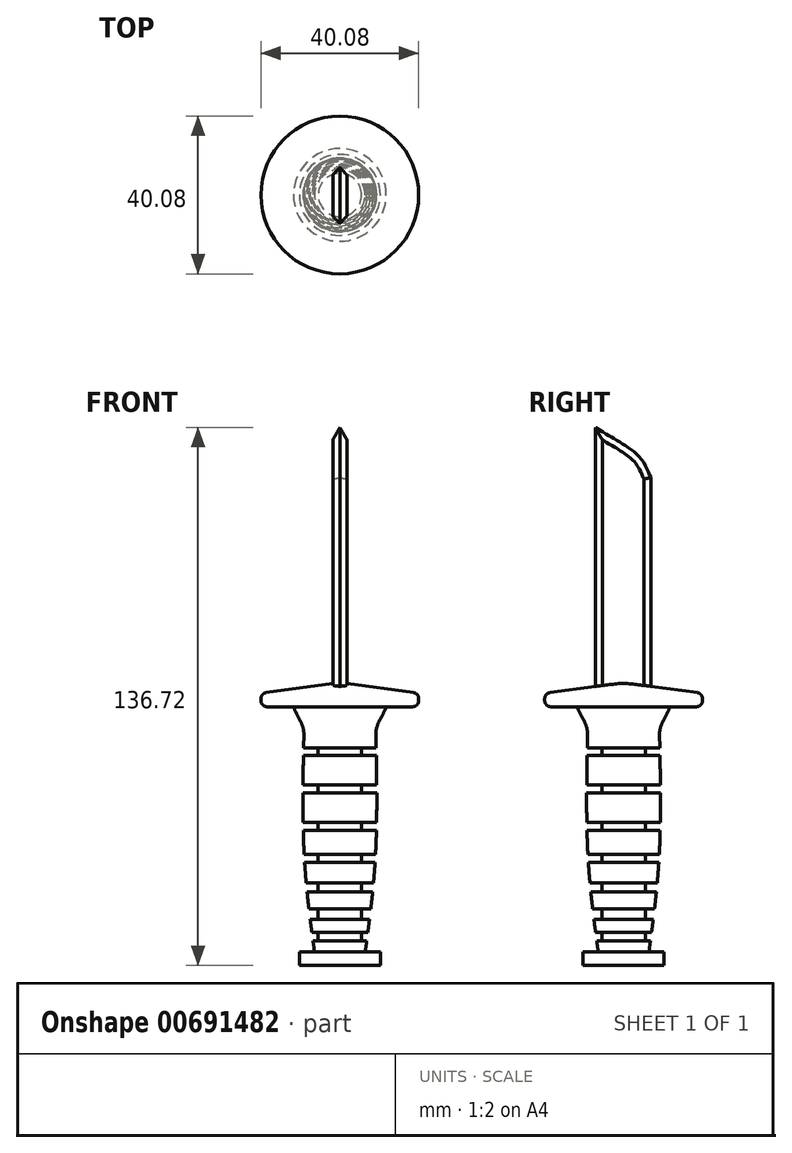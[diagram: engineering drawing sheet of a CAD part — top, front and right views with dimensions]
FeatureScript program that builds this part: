
annotation { "Feature Type Name" : "Feature", "Feature Type Description" : "" }
export const myFeature = defineFeature(function(context is Context, id is Id, definition is map)
    precondition{}
    {
        {
            var Q0;
            Q0=qCreatedBy(makeId("Front.planeOp"),FACE);
            var sketch = newSketch(context, id + "F0", { "sketchPlane" : qUnion([Q0])});
            skLineSegment(sketch, "E0", {"start": v(0, 79.4) * mm, "end": v(0, -77.48) * mm, "construction": true});
            skLineSegment(sketch, "E1", {"start": v(0, 41.4) * mm, "end": v(-13.25, 41.4) * mm});
            skLineSegment(sketch, "E2", {"start": v(-13.25, 41.4) * mm, "end": v(-13.25, 37.56) * mm});
            skLineSegment(sketch, "E3", {"start": v(-13.25, 37.56) * mm, "end": v(-9.06, 33.56) * mm});
            skFitSpline(sketch, "E4", {"points": [v(-9.06, 33.56) * mm, v(-9.06, 0) * mm, v(-6.45, -24.67) * mm], "startDerivative": vector(-1.52, -64.84) * mm, "endDerivative": vector(6.96, -51.26) * mm});
            skLineSegment(sketch, "E5", {"start": v(-6.45, -24.67) * mm, "end": v(-10.28, -24.67) * mm});
            skLineSegment(sketch, "E6", {"start": v(-10.28, -24.67) * mm, "end": v(-10.28, -28.15) * mm});
            skLineSegment(sketch, "E7", {"start": v(-10.28, -28.15) * mm, "end": v(0, -28.15) * mm});
            skLineSegment(sketch, "E8", {"start": v(0, -28.15) * mm, "end": v(0, 41.4) * mm});
            skSolve(sketch);
        }
        {
            var Q0;
            Q0 = qSketchRegion(id + "F0", true);
            var Q1;
            Q1=sQuery(id+"F0.wireOp",EDGE,"E8");
            revolve(context, id + "F1", {"entities" : qUnion([Q0]), "axis" : qUnion([Q1]), "revolveType" : RevolveType.FULL});
        }
        {
            var Q0;
            Q0=qCreatedBy(makeId("Right.planeOp"),FACE);
            var sketch = newSketch(context, id + "F2", { "sketchPlane" : qUnion([Q0])});
            skLineSegment(sketch, "E9", {"start": v(7.44, 35.34) * mm, "end": v(7.44, 95.92) * mm});
            skFitSpline(sketch, "E10", {"points": [v(7.44, 95.92) * mm, v(4.1, 101.72) * mm, v(-7.71, 109.53) * mm], "startDerivative": vector(-6.13, 12.4) * mm, "endDerivative": vector(-14.92, 10.78) * mm});
            skLineSegment(sketch, "E11", {"start": v(-7.71, 109.53) * mm, "end": v(-7.71, 35.27) * mm});
            skLineSegment(sketch, "E12", {"start": v(-7.71, 35.27) * mm, "end": v(7.44, 35.34) * mm});
            skSolve(sketch);
        }
        {
            var Q0;
            Q0 = qSketchRegion(id + "F2", true);
            extrude(context, id + "F3", {"entities" : qUnion([Q0]), "operationType" : NewBodyOperationType.ADD, "endBound" : BoundingType.SYMMETRIC, "depth" : 3.56 * mm, "offsetDistance" : 25.4 * mm});
        }
        {
            var Q0;
            Q0=makeQuery(id+"F3.opExtrude","CAP_EDGE",EDGE,{"disambiguationData":[OSD([sQuery(id+"F2.wireOp",EDGE,"E9")])],"isStart":true});
            var Q1;
            Q1=makeQuery(id+"F3.opExtrude","CAP_EDGE",EDGE,{"disambiguationData":[OSD([sQuery(id+"F2.wireOp",EDGE,"E9")])],"isStart":false});
            chamfer(context, id + "F4", {"entities" : qUnion([Q0, Q1]), "width" : 2.3 * mm, "tangentPropagation" : true});
        }
        {
            var Q0;
            Q0=makeQuery(id+"F3.opExtrude","CAP_EDGE",EDGE,{"disambiguationData":[OSD([sQuery(id+"F2.wireOp",EDGE,"E10")])],"isStart":true});
            var Q1;
            Q1=makeQuery(id+"F3.opExtrude","CAP_EDGE",EDGE,{"disambiguationData":[OSD([sQuery(id+"F2.wireOp",EDGE,"E10")])],"isStart":false});
            chamfer(context, id + "F5", {"entities" : qUnion([Q0, Q1]), "width" : 2.3 * mm, "tangentPropagation" : true});
        }
        {
            var Q0;
            Q0=makeQuery(id+"F3.opExtrude","CAP_EDGE",EDGE,{"disambiguationData":[OSD([sQuery(id+"F2.wireOp",EDGE,"E11")])],"isStart":false});
            var Q1;
            Q1=makeQuery(id+"F3.opExtrude","CAP_EDGE",EDGE,{"disambiguationData":[OSD([sQuery(id+"F2.wireOp",EDGE,"E11")])],"isStart":true});
            chamfer(context, id + "F6", {"entities" : qUnion([Q0, Q1]), "width" : 2.3 * mm, "tangentPropagation" : true});
        }
        {
            var Q0;
            Q0=qCreatedBy(makeId("Front.planeOp"),FACE);
            var sketch = newSketch(context, id + "F7", { "sketchPlane" : qUnion([Q0])});
            skLineSegment(sketch, "E13.bottom", {"start": v(-12.37, 27.05) * mm, "end": v(-5.5, 27.05) * mm});
            skLineSegment(sketch, "E13.top", {"start": v(-12.37, 25.15) * mm, "end": v(-5.5, 25.15) * mm});
            skLineSegment(sketch, "E13.left", {"start": v(-12.37, 27.05) * mm, "end": v(-12.37, 25.15) * mm});
            skLineSegment(sketch, "E13.right", {"start": v(-5.5, 27.05) * mm, "end": v(-5.5, 25.15) * mm});
            skLineSegment(sketch, "E14.bottom", {"start": v(-12.37, 17.75) * mm, "end": v(-5.5, 17.75) * mm});
            skLineSegment(sketch, "E14.top", {"start": v(-12.37, 15.74) * mm, "end": v(-5.5, 15.74) * mm});
            skLineSegment(sketch, "E14.left", {"start": v(-12.37, 17.75) * mm, "end": v(-12.37, 15.74) * mm});
            skLineSegment(sketch, "E14.right", {"start": v(-5.5, 17.75) * mm, "end": v(-5.5, 15.74) * mm});
            skLineSegment(sketch, "E15.bottom", {"start": v(-12.37, 8.23) * mm, "end": v(-5.5, 8.23) * mm});
            skLineSegment(sketch, "E15.top", {"start": v(-12.37, 6.12) * mm, "end": v(-5.5, 6.12) * mm});
            skLineSegment(sketch, "E15.left", {"start": v(-12.37, 8.23) * mm, "end": v(-12.37, 6.12) * mm});
            skLineSegment(sketch, "E15.right", {"start": v(-5.5, 8.23) * mm, "end": v(-5.5, 6.12) * mm});
            skLineSegment(sketch, "E16.bottom", {"start": v(-12.37, 0) * mm, "end": v(-5.5, 0) * mm});
            skLineSegment(sketch, "E16.top", {"start": v(-12.37, -2.02) * mm, "end": v(-5.5, -2.02) * mm});
            skLineSegment(sketch, "E16.left", {"start": v(-12.37, 0) * mm, "end": v(-12.37, -2.02) * mm});
            skLineSegment(sketch, "E16.right", {"start": v(-5.5, 0) * mm, "end": v(-5.5, -2.02) * mm});
            skLineSegment(sketch, "E17.bottom", {"start": v(-12.37, -7.2) * mm, "end": v(-5.5, -7.2) * mm});
            skLineSegment(sketch, "E17.top", {"start": v(-12.37, -9.42) * mm, "end": v(-5.5, -9.42) * mm});
            skLineSegment(sketch, "E17.left", {"start": v(-12.37, -7.2) * mm, "end": v(-12.37, -9.42) * mm});
            skLineSegment(sketch, "E17.right", {"start": v(-5.5, -7.2) * mm, "end": v(-5.5, -9.42) * mm});
            skLineSegment(sketch, "E18.bottom", {"start": v(-12.37, -13.76) * mm, "end": v(-5.5, -13.76) * mm});
            skLineSegment(sketch, "E18.top", {"start": v(-12.37, -16.4) * mm, "end": v(-5.5, -16.4) * mm});
            skLineSegment(sketch, "E18.left", {"start": v(-12.37, -13.76) * mm, "end": v(-12.37, -16.4) * mm});
            skLineSegment(sketch, "E18.right", {"start": v(-5.5, -13.76) * mm, "end": v(-5.5, -16.4) * mm});
            skLineSegment(sketch, "E19.bottom", {"start": v(-12.37, -19.79) * mm, "end": v(-5.5, -19.79) * mm});
            skLineSegment(sketch, "E19.top", {"start": v(-12.37, -21.9) * mm, "end": v(-5.5, -21.9) * mm});
            skLineSegment(sketch, "E19.left", {"start": v(-12.37, -19.79) * mm, "end": v(-12.37, -21.9) * mm});
            skLineSegment(sketch, "E19.right", {"start": v(-5.5, -19.79) * mm, "end": v(-5.5, -21.9) * mm});
            skLineSegment(sketch, "E20", {"start": v(0, 30.96) * mm, "end": v(0, -34.06) * mm, "construction": true});
            skLineSegment(sketch, "E21", {"start": v(0, 34.24) * mm, "end": v(0, -24.86) * mm});
            skSolve(sketch);
        }
        {
            var Q0;
            Q0 = qSketchRegion(id + "F7", true);
            var Q1;
            Q1=sQuery(id+"F7.wireOp",EDGE,"E21");
            revolve(context, id + "F8", {"operationType" : NewBodyOperationType.REMOVE, "entities" : qUnion([Q0]), "axis" : qUnion([Q1]), "revolveType" : RevolveType.FULL, "oppositeDirection" : true});
        }
        {
            var Q0;
            Q0=qCreatedBy(makeId("Front.planeOp"),FACE);
            var sketch = newSketch(context, id + "F9", { "sketchPlane" : qUnion([Q0])});
            skLineSegment(sketch, "E22", {"start": v(0, 43.74) * mm, "end": v(-20.04, 40.98) * mm});
            skLineSegment(sketch, "E23", {"start": v(-20.04, 40.98) * mm, "end": v(-20.04, 37.58) * mm});
            skLineSegment(sketch, "E24", {"start": v(-20.04, 37.58) * mm, "end": v(0, 37.58) * mm});
            skLineSegment(sketch, "E25", {"start": v(0, 37.58) * mm, "end": v(0, 43.74) * mm});
            skLineSegment(sketch, "E26", {"start": v(0, 55.5) * mm, "end": v(0, 14.51) * mm, "construction": true});
            skSolve(sketch);
        }
        {
            var Q0;
            Q0 = qSketchRegion(id + "F9", true);
            var Q1;
            Q1=sQuery(id+"F9.wireOp",EDGE,"E25");
            revolve(context, id + "F10", {"operationType" : NewBodyOperationType.ADD, "entities" : qUnion([Q0]), "axis" : qUnion([Q1]), "revolveType" : RevolveType.FULL});
        }
        {
            var Q0;
            Q0=makeQuery(id+"F10.opRevolve","SWEPT_EDGE",EDGE,{"disambiguationData":[OSD([sQuery(id+"F9.wireOp",EDGE,"E22"),sQuery(id+"F9.wireOp",EDGE,"E23")])]});
            var Q1;
            Q1=makeQuery(id+"F10.opRevolve","SWEPT_EDGE",EDGE,{"disambiguationData":[OSD([sQuery(id+"F9.wireOp",EDGE,"E23"),sQuery(id+"F9.wireOp",EDGE,"E24")])]});
            fillet(context, id + "F11", {"entities" : qUnion([Q0, Q1]), "radius" : 1.53 * mm, "tangentPropagation" : true, "allowEdgeOverflow" : false});
        }
        {
            var Q0;
            Q0=makeQuery(id+"F1.opRevolve","SWEPT_EDGE",EDGE,{"disambiguationData":[OSD([sQuery(id+"F0.wireOp",EDGE,"E3"),sQuery(id+"F0.wireOp",EDGE,"E4")])]});
            fillet(context, id + "F12", {"entities" : qUnion([Q0]), "radius" : 7.4 * mm, "tangentPropagation" : true, "allowEdgeOverflow" : false});
        }
        {
            var Q0;
            Q0=makeQuery(id+"F1.opRevolve","SWEPT_EDGE",EDGE,{"disambiguationData":[OSD([sQuery(id+"F0.wireOp",EDGE,"E2"),sQuery(id+"F0.wireOp",EDGE,"E3")])]});
            fillet(context, id + "F13", {"entities" : qUnion([Q0]), "radius" : 22.42 * mm, "tangentPropagation" : true, "allowEdgeOverflow" : false});
        }
    });
